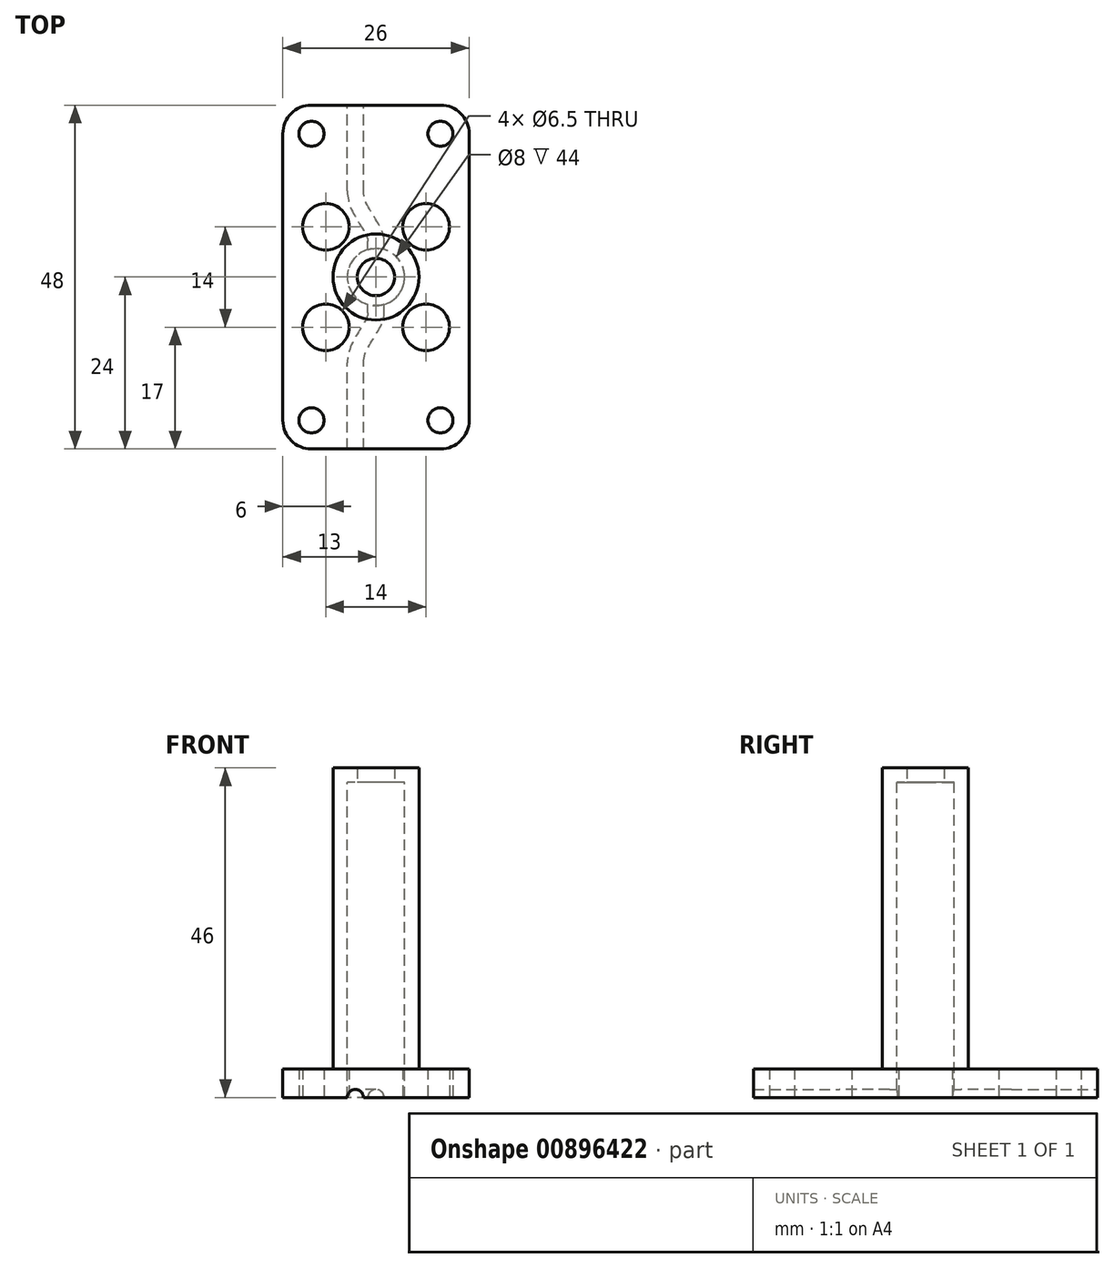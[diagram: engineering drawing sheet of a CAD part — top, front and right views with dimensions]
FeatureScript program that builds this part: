
annotation { "Feature Type Name" : "Feature", "Feature Type Description" : "" }
export const myFeature = defineFeature(function(context is Context, id is Id, definition is map)
    precondition{}
    {
        {
            var Q0;
            Q0=qCreatedBy(makeId("Top.planeOp"),FACE);
            var sketch = newSketch(context, id + "F0", { "sketchPlane" : qUnion([Q0])});
            skCircle(sketch, "E0", {"center": v(-7, 7) * mm, "radius": 3.25 * mm});
            skCircle(sketch, "E1", {"center": v(7, 7) * mm, "radius": 3.25 * mm});
            skCircle(sketch, "E2", {"center": v(7, -7) * mm, "radius": 3.25 * mm});
            skCircle(sketch, "E3", {"center": v(-7, -7) * mm, "radius": 3.25 * mm});
            skCircle(sketch, "E4", {"center": v(-9, 20) * mm, "radius": 1.75 * mm});
            skCircle(sketch, "E5", {"center": v(9, 20) * mm, "radius": 1.75 * mm});
            skCircle(sketch, "E6", {"center": v(9, -20) * mm, "radius": 1.75 * mm});
            skCircle(sketch, "E7", {"center": v(-9, -20) * mm, "radius": 1.75 * mm});
            skArc(sketch, "E8", {"start": v(-9, -24) * mm, "mid": v(-11.83, -22.83) * mm, "end": v(-13, -20) * mm});
            skArc(sketch, "E9", {"start": v(-13, 20) * mm, "mid": v(-11.83, 22.83) * mm, "end": v(-9, 24) * mm});
            skArc(sketch, "E10", {"start": v(9, 24) * mm, "mid": v(11.83, 22.83) * mm, "end": v(13, 20) * mm});
            skArc(sketch, "E11", {"start": v(13, -20) * mm, "mid": v(11.83, -22.83) * mm, "end": v(9, -24) * mm});
            skLineSegment(sketch, "E12", {"start": v(-13, -20) * mm, "end": v(-13, 20) * mm});
            skLineSegment(sketch, "E13", {"start": v(-9, 24) * mm, "end": v(9, 24) * mm});
            skLineSegment(sketch, "E14", {"start": v(13, 20) * mm, "end": v(13, -20) * mm});
            skLineSegment(sketch, "E15", {"start": v(9, -24) * mm, "end": v(-9, -24) * mm});
            skSolve(sketch);
        }
        {
            var Q0;
            Q0=qSketchRegion(id+"F0",true);
            extrude(context, id + "F1", {"entities" : qUnion([Q0]), "depth" : 4 * mm, "offsetDistance" : 25 * mm});
        }
        {
            var Q0;
            Q0=makeQuery(id+"F1.opExtrude","CAP_FACE",FACE,{"disambiguationData":[OSD([sQuery(id+"F0.wireOp",EDGE,"E0"),sQuery(id+"F0.wireOp",EDGE,"E1"),sQuery(id+"F0.wireOp",EDGE,"E2"),sQuery(id+"F0.wireOp",EDGE,"E3"),sQuery(id+"F0.wireOp",EDGE,"E4"),sQuery(id+"F0.wireOp",EDGE,"E5"),sQuery(id+"F0.wireOp",EDGE,"E6"),sQuery(id+"F0.wireOp",EDGE,"E7"),sQuery(id+"F0.wireOp",EDGE,"E8"),sQuery(id+"F0.wireOp",EDGE,"E9"),sQuery(id+"F0.wireOp",EDGE,"E10"),sQuery(id+"F0.wireOp",EDGE,"E11"),sQuery(id+"F0.wireOp",EDGE,"E12"),sQuery(id+"F0.wireOp",EDGE,"E13"),sQuery(id+"F0.wireOp",EDGE,"E14"),sQuery(id+"F0.wireOp",EDGE,"E15")])],"isStart":false});
            var sketch = newSketch(context, id + "F2", { "sketchPlane" : qUnion([Q0])});
            skCircle(sketch, "E16", {"center": v(0, 0) * mm, "radius": 6 * mm});
            skSolve(sketch);
        }
        {
            var Q0;
            Q0=qSketchRegion(id+"F2",true);
            extrude(context, id + "F3", {"entities" : qUnion([Q0]), "operationType" : NewBodyOperationType.ADD, "depth" : 40 * mm, "offsetDistance" : 25 * mm});
        }
        {
            var Q0;
            Q0=makeQuery(id+"F3.opExtrude","CAP_FACE",FACE,{"disambiguationData":[OSD([sQuery(id+"F2.wireOp",EDGE,"E16")])],"isStart":false});
            var sketch = newSketch(context, id + "F4", { "sketchPlane" : qUnion([Q0])});
            skCircle(sketch, "E17", {"center": v(0, 0) * mm, "radius": 4 * mm});
            skSolve(sketch);
        }
        {
            var Q0;
            Q0=qSketchRegion(id+"F4",true);
            extrude(context, id + "F5", {"entities" : qUnion([Q0]), "depth" : -50 * mm, "offsetDistance" : 25 * mm});
        }
        {
            var Q0;
            Q0=makeQuery(id+"F5.opExtrude","SWEPT_BODY",BODY,{"disambiguationData":[OSD([sQuery(id+"F4.wireOp",EDGE,"E17")])]});
            var Q1;
            Q1=makeQuery(id+"F1.opExtrude","SWEPT_BODY",BODY,{"disambiguationData":[OSD([sQuery(id+"F0.wireOp",EDGE,"E0"),sQuery(id+"F0.wireOp",EDGE,"E1"),sQuery(id+"F0.wireOp",EDGE,"E2"),sQuery(id+"F0.wireOp",EDGE,"E3"),sQuery(id+"F0.wireOp",EDGE,"E4"),sQuery(id+"F0.wireOp",EDGE,"E5"),sQuery(id+"F0.wireOp",EDGE,"E6"),sQuery(id+"F0.wireOp",EDGE,"E7"),sQuery(id+"F0.wireOp",EDGE,"E8"),sQuery(id+"F0.wireOp",EDGE,"E9"),sQuery(id+"F0.wireOp",EDGE,"E10"),sQuery(id+"F0.wireOp",EDGE,"E11"),sQuery(id+"F0.wireOp",EDGE,"E12"),sQuery(id+"F0.wireOp",EDGE,"E13"),sQuery(id+"F0.wireOp",EDGE,"E14"),sQuery(id+"F0.wireOp",EDGE,"E15")])]});
            booleanBodies(context, id + "F6", {"operationType" : BooleanOperationType.SUBTRACTION, "tools" : qUnion([Q0]), "targets" : qUnion([Q1])});
        }
        {
            var Q0;
            Q0=makeQuery(id+"F3.opExtrude","CAP_FACE",FACE,{"disambiguationData":[OSD([sQuery(id+"F2.wireOp",EDGE,"E16")])],"isStart":false});
            var sketch = newSketch(context, id + "F7", { "sketchPlane" : qUnion([Q0])});
            skCircle(sketch, "E18", {"center": v(0, 0) * mm, "radius": 6 * mm});
            skCircle(sketch, "E19", {"center": v(0, 0) * mm, "radius": 2.6 * mm});
            skSolve(sketch);
        }
        {
            var Q0;
            Q0=qSketchRegion(id+"F7",true);
            extrude(context, id + "F8", {"entities" : qUnion([Q0]), "operationType" : NewBodyOperationType.ADD, "depth" : 2 * mm, "offsetDistance" : 25 * mm});
        }
        {
            var Q0;
            Q0=makeQuery(id+"F1.opExtrude","CAP_FACE",FACE,{"disambiguationData":[OSD([sQuery(id+"F0.wireOp",EDGE,"E0"),sQuery(id+"F0.wireOp",EDGE,"E1"),sQuery(id+"F0.wireOp",EDGE,"E2"),sQuery(id+"F0.wireOp",EDGE,"E3"),sQuery(id+"F0.wireOp",EDGE,"E4"),sQuery(id+"F0.wireOp",EDGE,"E5"),sQuery(id+"F0.wireOp",EDGE,"E6"),sQuery(id+"F0.wireOp",EDGE,"E7"),sQuery(id+"F0.wireOp",EDGE,"E8"),sQuery(id+"F0.wireOp",EDGE,"E9"),sQuery(id+"F0.wireOp",EDGE,"E10"),sQuery(id+"F0.wireOp",EDGE,"E11"),sQuery(id+"F0.wireOp",EDGE,"E12"),sQuery(id+"F0.wireOp",EDGE,"E13"),sQuery(id+"F0.wireOp",EDGE,"E14"),sQuery(id+"F0.wireOp",EDGE,"E15")])],"isStart":true});
            var sketch = newSketch(context, id + "F9", { "sketchPlane" : qUnion([Q0])});
            skLineSegment(sketch, "E20.bottom", {"start": v(-4, -24) * mm, "end": v(-1.75, -24) * mm});
            skLineSegment(sketch, "E20.top", {"start": v(-4, -12) * mm, "end": v(-1.75, -12) * mm});
            skLineSegment(sketch, "E20.left", {"start": v(-4, -24) * mm, "end": v(-4, -12) * mm});
            skLineSegment(sketch, "E20.right", {"start": v(-1.75, -24) * mm, "end": v(-1.75, -12) * mm});
            skLineSegment(sketch, "E21.bottom", {"start": v(-4, 24) * mm, "end": v(-1.75, 24) * mm});
            skLineSegment(sketch, "E21.top", {"start": v(-4, 12) * mm, "end": v(-1.75, 12) * mm});
            skLineSegment(sketch, "E21.left", {"start": v(-4, 24) * mm, "end": v(-4, 12) * mm});
            skLineSegment(sketch, "E21.right", {"start": v(-1.75, 24) * mm, "end": v(-1.75, 12) * mm});
            skLineSegment(sketch, "E22.bottom", {"start": v(1.13, 5) * mm, "end": v(-1.12, 5) * mm});
            skLineSegment(sketch, "E22.top", {"start": v(1.13, -5) * mm, "end": v(-1.13, -5) * mm});
            skLineSegment(sketch, "E22.left", {"start": v(1.13, 5) * mm, "end": v(1.13, -5) * mm});
            skLineSegment(sketch, "E22.right", {"start": v(-1.13, 5) * mm, "end": v(-1.13, -5) * mm});
            skPoint(sketch, "E22.middle", {"position": v(0, 0) * mm});
            skFitSpline(sketch, "E23", {"points": [v(-4, 12) * mm, v(-1.13, 5) * mm], "startDerivative": vector(0, -7.36) * mm, "endDerivative": vector(0, -7.36) * mm});
            skFitSpline(sketch, "E24", {"points": [v(-1.75, 12) * mm, v(1.12, 5) * mm], "startDerivative": vector(0, -7.36) * mm, "endDerivative": vector(0, -7.36) * mm});
            skFitSpline(sketch, "E25", {"points": [v(-4, -12) * mm, v(-1.13, -5) * mm], "startDerivative": vector(0, 7.23) * mm, "endDerivative": vector(0, 7.23) * mm});
            skFitSpline(sketch, "E26", {"points": [v(-1.75, -12) * mm, v(1.12, -5) * mm], "startDerivative": vector(0, 7.23) * mm, "endDerivative": vector(0, 7.23) * mm});
            skSolve(sketch);
        }
        {
            var Q0;
            Q0=makeQuery(id+"F1.opExtrude","SWEPT_FACE",FACE,{"disambiguationData":[OSD([sQuery(id+"F0.wireOp",EDGE,"E15")])]});
            var sketch = newSketch(context, id + "F10", { "sketchPlane" : qUnion([Q0])});
            skCircle(sketch, "E27", {"center": v(-2.87, 0) * mm, "radius": 1.13 * mm});
            skSolve(sketch);
        }
        {
            var Q0;
            {var subQ0=sQuery(id+"F10.wireOp",EDGE,"E27");var subQ1=makeQuery(id+"F1.opExtrude","CAP_EDGE",EDGE,{"disambiguationData":[OSD([sQuery(id+"F0.wireOp",EDGE,"E15")])],"isStart":true});var subQ2=makeQuery(id+"F10.imprint","INTERSECT",VERTEX,{"disambiguationData":[OD(0.0)],"derivedFrom":[subQ1,subQ0]});Q0=makeQuery(id+"F10.imprint","IMPRINT",FACE,{"disambiguationData":[TD([[makeQuery(id+"F10.imprint","IMPRINT",EDGE,{"disambiguationData":[TD([[subQ2,-1.0]])],"derivedFrom":subQ0}),1.0]])]});}
            var Q1;
            {var subQ0=sQuery(id+"F10.wireOp",EDGE,"E27");var subQ1=makeQuery(id+"F1.opExtrude","CAP_EDGE",EDGE,{"disambiguationData":[OSD([sQuery(id+"F0.wireOp",EDGE,"E15")])],"isStart":true});var subQ2=makeQuery(id+"F10.imprint","INTERSECT",VERTEX,{"disambiguationData":[OD(0.0)],"derivedFrom":[subQ1,subQ0]});Q1=makeQuery(id+"F10.imprint","IMPRINT",FACE,{"disambiguationData":[TD([[makeQuery(id+"F10.imprint","IMPRINT",EDGE,{"disambiguationData":[TD([[subQ2,1.0]])],"derivedFrom":subQ0}),1.0]])]});}
            var Q2;
            Q2=sQuery(id+"F9.wireOp",EDGE,"E21.right");
            var Q3;
            Q3=sQuery(id+"F9.wireOp",EDGE,"E24");
            var Q4;
            Q4=sQuery(id+"F9.wireOp",EDGE,"E22.left");
            var Q5;
            Q5=sQuery(id+"F9.wireOp",EDGE,"E26");
            var Q6;
            Q6=sQuery(id+"F9.wireOp",EDGE,"E20.right");
            sweep(context, id + "F11", {"profiles" : qUnion([Q0, Q1]), "path" : qUnion([Q2, Q3, Q4, Q5, Q6])});
        }
        {
            var Q0;
            Q0=makeQuery(id+"F11.opSweep","SWEPT_BODY",BODY,{"disambiguationData":[OSD([sQuery(id+"F9.wireOp",EDGE,"E20.right"),sQuery(id+"F10.wireOp",EDGE,"E27")])]});
            var Q1;
            Q1=makeQuery(id+"F1.opExtrude","SWEPT_BODY",BODY,{"disambiguationData":[OSD([sQuery(id+"F0.wireOp",EDGE,"E0"),sQuery(id+"F0.wireOp",EDGE,"E1"),sQuery(id+"F0.wireOp",EDGE,"E2"),sQuery(id+"F0.wireOp",EDGE,"E3"),sQuery(id+"F0.wireOp",EDGE,"E4"),sQuery(id+"F0.wireOp",EDGE,"E5"),sQuery(id+"F0.wireOp",EDGE,"E6"),sQuery(id+"F0.wireOp",EDGE,"E7"),sQuery(id+"F0.wireOp",EDGE,"E8"),sQuery(id+"F0.wireOp",EDGE,"E9"),sQuery(id+"F0.wireOp",EDGE,"E10"),sQuery(id+"F0.wireOp",EDGE,"E11"),sQuery(id+"F0.wireOp",EDGE,"E12"),sQuery(id+"F0.wireOp",EDGE,"E13"),sQuery(id+"F0.wireOp",EDGE,"E14"),sQuery(id+"F0.wireOp",EDGE,"E15")])]});
            booleanBodies(context, id + "F12", {"operationType" : BooleanOperationType.SUBTRACTION, "tools" : qUnion([Q0]), "targets" : qUnion([Q1])});
        }
    });
